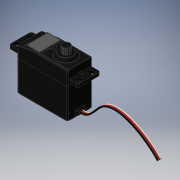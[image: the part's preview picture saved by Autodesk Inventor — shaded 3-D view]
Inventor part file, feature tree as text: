
AUTODESK INVENTOR PART (.ipt)
format: ipt  version: 2016 (Build 200138000, 138)  size: 628,224 bytes
history: native  units: in
note: dims shown in document units (in); Inventor stores cm internally (conversion verified against a paired STEP export)
features: other x1, sweep x1, fillet x1
ambient origin geometry x8: Origin, YZ Plane, XZ Plane, XY Plane, X Axis, Y Axis, Z Axis, Center Point
bodies: Solid1 (feature_tree), Solid2 (feature_tree), Solid3 (feature_tree)
feature tree (3):
  other  "Split1[2]"
  sweep  "Sweep1"
  fillet  "Fillet5"  [1 undecoded]
note: 1 required parameter value undecoded (feature->parameter linkage not recoverable at this tier; creation-order binding heuristic only, values carry confidence <= 0.55)
